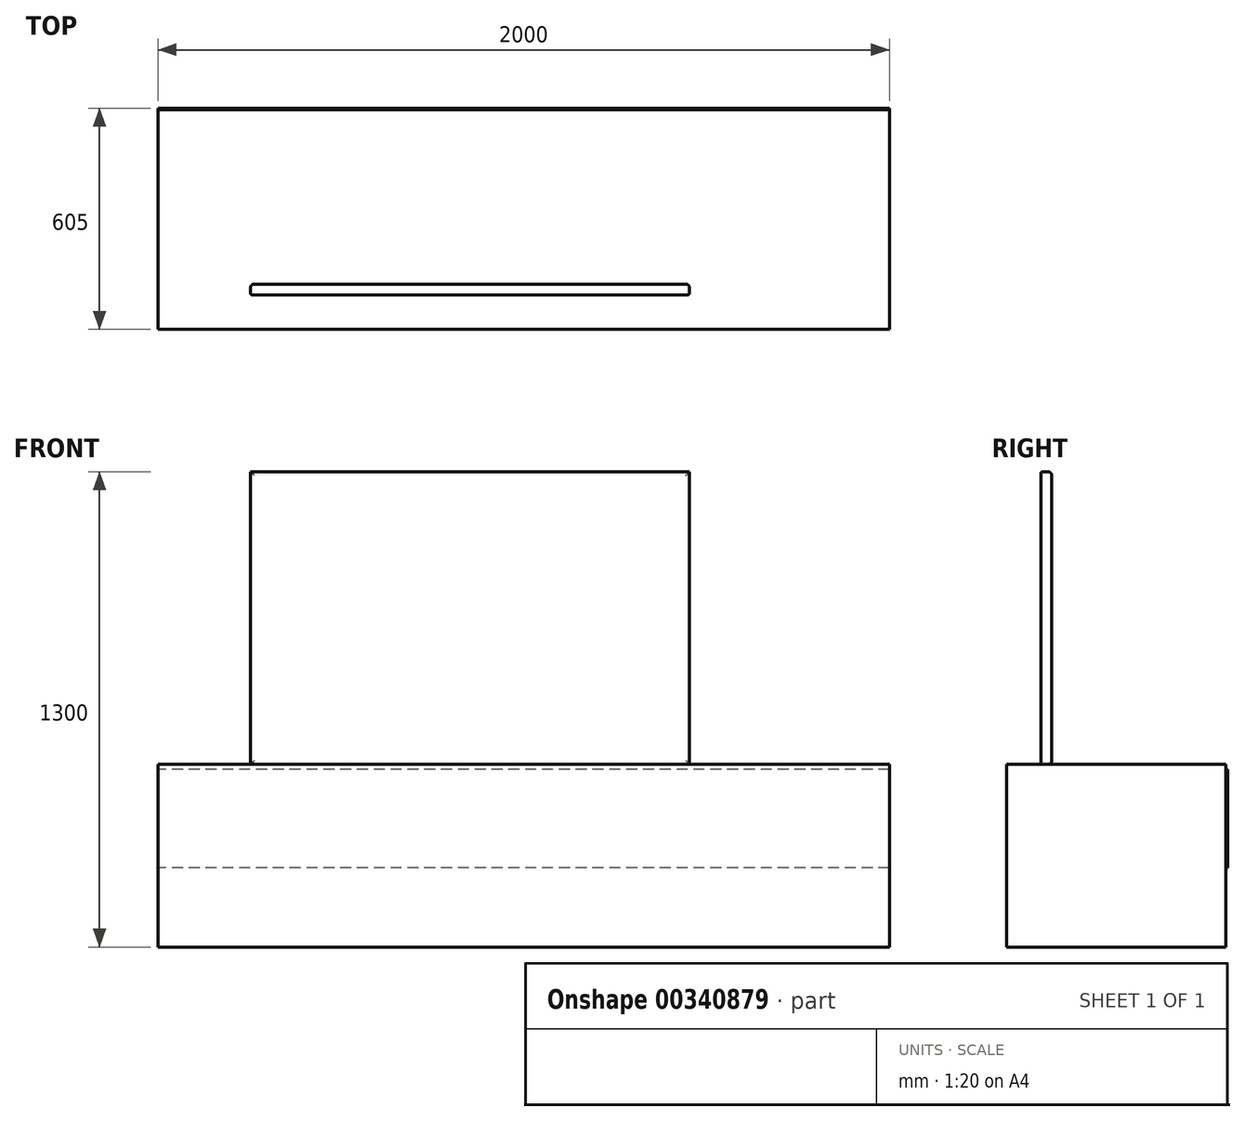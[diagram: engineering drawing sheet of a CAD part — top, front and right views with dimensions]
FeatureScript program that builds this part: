
annotation { "Feature Type Name" : "Feature", "Feature Type Description" : "" }
export const myFeature = defineFeature(function(context is Context, id is Id, definition is map)
    precondition{}
    {
        {
            var Q0;
            Q0=qCreatedBy(makeId("Top.planeOp"),FACE);
            var sketch = newSketch(context, id + "F0", { "sketchPlane" : qUnion([Q0])});
            skLineSegment(sketch, "E0.bottom", {"start": v(-96.87, 555.82) * mm, "end": v(1903.13, 555.82) * mm});
            skLineSegment(sketch, "E0.top", {"start": v(-96.87, -44.18) * mm, "end": v(1903.13, -44.18) * mm});
            skLineSegment(sketch, "E0.left", {"start": v(-96.87, 555.82) * mm, "end": v(-96.87, -44.18) * mm});
            skLineSegment(sketch, "E0.right", {"start": v(1903.13, 555.82) * mm, "end": v(1903.13, -44.18) * mm});
            skSolve(sketch);
        }
        {
            var Q0;
            Q0=makeQuery(id+"F0.imprint","IMPRINT",FACE,{"disambiguationData":[TD([[makeQuery(id+"F0.imprint","IMPRINT",EDGE,{"derivedFrom":sQuery(id+"F0.wireOp",EDGE,"E0.bottom")}),-1.0]])]});
            extrude(context, id + "F1", {"entities" : qUnion([Q0]), "depth" : 500 * mm});
        }
        {
            var Q0;
            Q0=makeQuery(id+"F1.opExtrude","CAP_FACE",FACE,{"disambiguationData":[OSD([sQuery(id+"F0.wireOp",EDGE,"E0.bottom"),sQuery(id+"F0.wireOp",EDGE,"E0.top"),sQuery(id+"F0.wireOp",EDGE,"E0.left"),sQuery(id+"F0.wireOp",EDGE,"E0.right")])],"isStart":false});
            var sketch = newSketch(context, id + "F2", { "sketchPlane" : qUnion([Q0])});
            skLineSegment(sketch, "E1.bottom", {"start": v(156.04, 79.49) * mm, "end": v(1356.04, 79.49) * mm});
            skLineSegment(sketch, "E1.top", {"start": v(156.04, 49.49) * mm, "end": v(1356.04, 49.49) * mm});
            skLineSegment(sketch, "E1.left", {"start": v(156.04, 79.49) * mm, "end": v(156.04, 49.49) * mm});
            skLineSegment(sketch, "E1.right", {"start": v(1356.04, 79.49) * mm, "end": v(1356.04, 49.49) * mm});
            skSolve(sketch);
        }
        {
            var Q0;
            Q0=makeQuery(id+"F2.imprint","IMPRINT",FACE,{"disambiguationData":[TD([[makeQuery(id+"F2.imprint","IMPRINT",EDGE,{"derivedFrom":sQuery(id+"F2.wireOp",EDGE,"E1.bottom")}),-1.0]])]});
            extrude(context, id + "F3", {"entities" : qUnion([Q0]), "depth" : 800 * mm});
        }
        {
            var Q0;
            Q0=makeQuery(id+"F3.opExtrude","SWEPT_FACE",FACE,{"disambiguationData":[OSD([sQuery(id+"F2.wireOp",EDGE,"E1.bottom")])]});
            fillet(context, id + "F4", {"entities" : qUnion([Q0]), "radius" : 10 * mm, "tangentPropagation" : true, "allowEdgeOverflow" : false});
        }
        {
            var Q0;
            Q0=makeQuery(id+"F3.opExtrude","SWEPT_FACE",FACE,{"disambiguationData":[OSD([sQuery(id+"F2.wireOp",EDGE,"E1.top")])]});
            fillet(context, id + "F5", {"entities" : qUnion([Q0]), "radius" : 5 * mm, "tangentPropagation" : true, "allowEdgeOverflow" : false});
        }
        {
            var Q0;
            Q0=makeQuery(id+"F1.opExtrude","SWEPT_FACE",FACE,{"disambiguationData":[OSD([sQuery(id+"F0.wireOp",EDGE,"E0.bottom")])]});
            var sketch = newSketch(context, id + "F6", { "sketchPlane" : qUnion([Q0])});
            skLineSegment(sketch, "E2.bottom", {"start": v(-1903.13, 485.88) * mm, "end": v(96.87, 485.88) * mm});
            skLineSegment(sketch, "E2.top", {"start": v(-1903.13, 216.2) * mm, "end": v(96.87, 216.2) * mm});
            skLineSegment(sketch, "E2.left", {"start": v(-1903.13, 485.88) * mm, "end": v(-1903.13, 216.2) * mm});
            skLineSegment(sketch, "E2.right", {"start": v(96.87, 485.88) * mm, "end": v(96.87, 216.2) * mm});
            skSolve(sketch);
        }
        {
            var Q0;
            Q0=makeQuery(id+"F6.imprint","IMPRINT",FACE,{"disambiguationData":[TD([[makeQuery(id+"F6.imprint","IMPRINT",EDGE,{"derivedFrom":sQuery(id+"F6.wireOp",EDGE,"E2.bottom")}),-1.0]])]});
            extrude(context, id + "F7", {"entities" : qUnion([Q0]), "depth" : 5 * mm});
        }
    });
